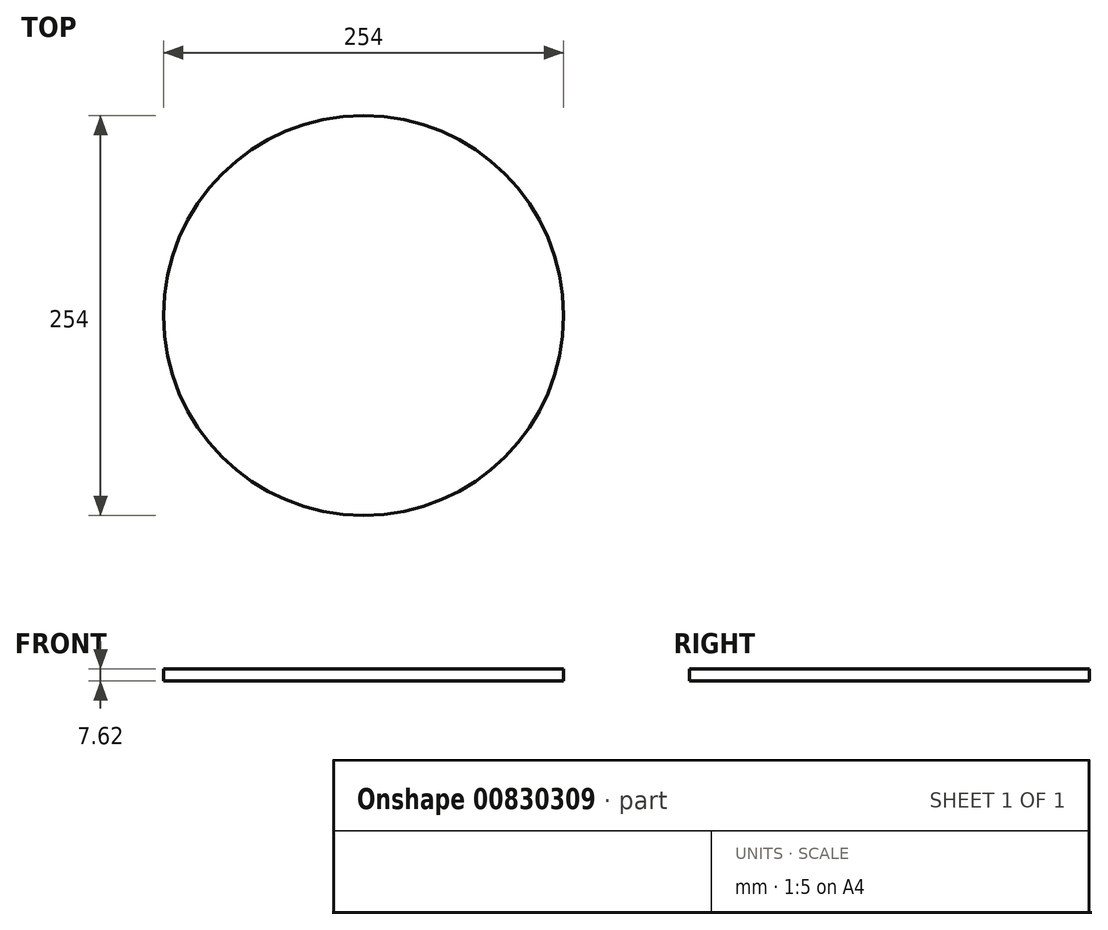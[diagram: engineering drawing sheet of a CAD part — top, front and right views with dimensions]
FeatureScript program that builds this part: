
annotation { "Feature Type Name" : "Feature", "Feature Type Description" : "" }
export const myFeature = defineFeature(function(context is Context, id is Id, definition is map)
    precondition{}
    {
        {
            var Q0;
            Q0=qCreatedBy(makeId("Top.planeOp"),FACE);
            var sketch = newSketch(context, id + "F0", { "sketchPlane" : qUnion([Q0])});
            skCircle(sketch, "E0", {"center": v(0, 0) * mm, "radius": 127 * mm});
            skSolve(sketch);
        }
        {
            var Q0;
            Q0 = qSketchRegion(id + "F0", true);
            extrude(context, id + "F1", {"entities" : qUnion([Q0]), "depth" : 7.62 * mm, "offsetDistance" : 25.4 * mm});
        }
    });
